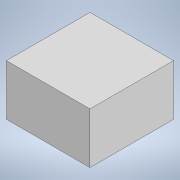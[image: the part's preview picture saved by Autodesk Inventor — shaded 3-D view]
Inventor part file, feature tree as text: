
AUTODESK INVENTOR PART (.ipt)
format: ipt  version: 2020 (Build 240168000, 168)  size: 100,864 bytes
history: native  units: mm
features: extrude x2, sketch x2
ambient origin geometry x8: Origin, YZ Plane, XZ Plane, XY Plane, X Axis, Y Axis, Z Axis, Center Point
bodies: Solid1 (feature_tree)
feature tree (4):
  extrude  "Extrusion1"  Depth=90.0mm
  extrude  "Extrusion2"  Depth=92.0mm
  sketch  "Sketch1"  dims[d0=90.0mm d1=90.0mm]
  sketch  "Sketch2"  dims[d2=55.0mm d3=0.0mm d4=92.0mm d5=92.0mm d6=1.0mm d7=0.0mm]
